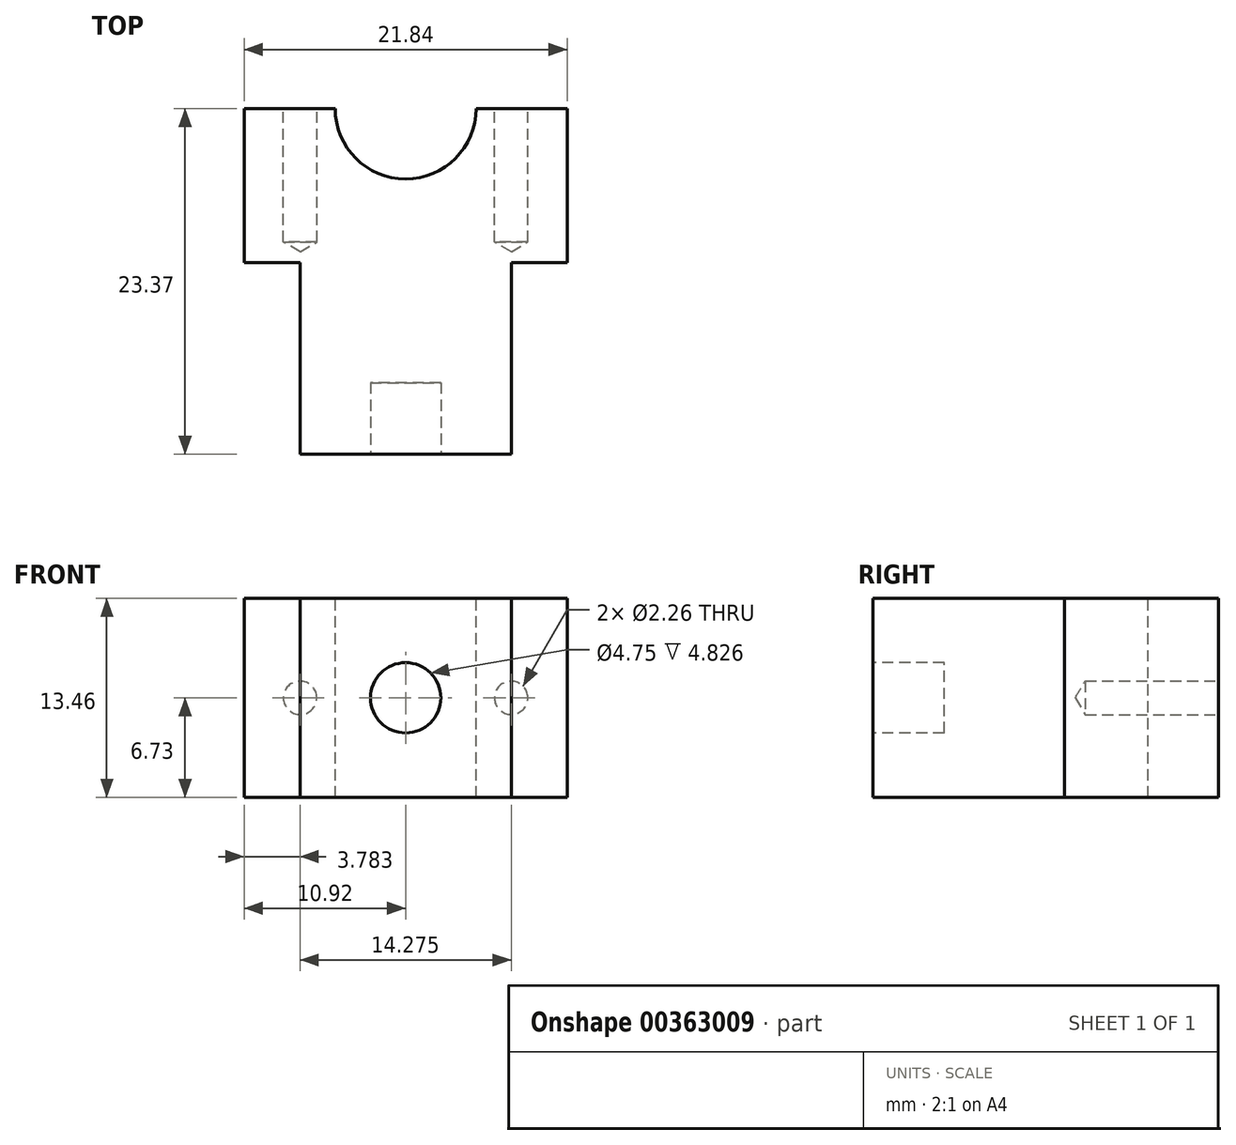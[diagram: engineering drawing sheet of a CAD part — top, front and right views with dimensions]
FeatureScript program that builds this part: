
annotation { "Feature Type Name" : "Feature", "Feature Type Description" : "" }
export const myFeature = defineFeature(function(context is Context, id is Id, definition is map)
    precondition{}
    {
        {
            var Q0;
            Q0=qCreatedBy(makeId("Front.planeOp"),FACE);
            var sketch = newSketch(context, id + "F0", { "sketchPlane" : qUnion([Q0])});
            skLineSegment(sketch, "E0.bottom", {"start": v(10.92, 6.73) * mm, "end": v(-10.92, 6.73) * mm});
            skLineSegment(sketch, "E0.top", {"start": v(10.92, -6.73) * mm, "end": v(-10.92, -6.73) * mm});
            skLineSegment(sketch, "E0.left", {"start": v(10.92, 6.73) * mm, "end": v(10.92, -6.73) * mm});
            skLineSegment(sketch, "E0.right", {"start": v(-10.92, 6.73) * mm, "end": v(-10.92, -6.73) * mm});
            skPoint(sketch, "E0.middle", {"position": v(0, 0) * mm});
            skSolve(sketch);
        }
        {
            var Q0;
            Q0=makeQuery(id+"F0.imprint","IMPRINT",FACE,{"disambiguationData":[TD([[makeQuery(id+"F0.imprint","IMPRINT",EDGE,{"derivedFrom":sQuery(id+"F0.wireOp",EDGE,"E0.bottom")}),1.0]])]});
            extrude(context, id + "F1", {"entities" : qUnion([Q0]), "depth" : 10.4 * mm});
        }
        {
            var Q0;
            Q0=makeQuery(id+"F1.opExtrude","CAP_FACE",FACE,{"disambiguationData":[OSD([sQuery(id+"F0.wireOp",EDGE,"E0.bottom"),sQuery(id+"F0.wireOp",EDGE,"E0.top"),sQuery(id+"F0.wireOp",EDGE,"E0.left"),sQuery(id+"F0.wireOp",EDGE,"E0.right")])],"isStart":false});
            var sketch = newSketch(context, id + "F2", { "sketchPlane" : qUnion([Q0])});
            skLineSegment(sketch, "E1.bottom", {"start": v(7.14, 6.73) * mm, "end": v(-7.14, 6.73) * mm});
            skLineSegment(sketch, "E1.top", {"start": v(7.14, -6.73) * mm, "end": v(-7.14, -6.73) * mm});
            skLineSegment(sketch, "E1.left", {"start": v(7.14, 6.73) * mm, "end": v(7.14, -6.73) * mm});
            skLineSegment(sketch, "E1.right", {"start": v(-7.14, 6.73) * mm, "end": v(-7.14, -6.73) * mm});
            skPoint(sketch, "E1.middle", {"position": v(0, 0) * mm});
            skSolve(sketch);
        }
        {
            var Q0;
            Q0=makeQuery(id+"F2.imprint","IMPRINT",FACE,{"disambiguationData":[TD([[makeQuery(id+"F2.imprint","IMPRINT",EDGE,{"derivedFrom":sQuery(id+"F2.wireOp",EDGE,"E1.bottom")}),1.0]])]});
            extrude(context, id + "F3", {"entities" : qUnion([Q0]), "operationType" : NewBodyOperationType.ADD, "depth" : 12.95 * mm});
        }
        {
            var Q0;
            Q0=makeQuery(id+"F3.opExtrude","CAP_FACE",FACE,{"disambiguationData":[OSD([sQuery(id+"F2.wireOp",EDGE,"E1.bottom"),sQuery(id+"F2.wireOp",EDGE,"E1.top"),sQuery(id+"F2.wireOp",EDGE,"E1.left"),sQuery(id+"F2.wireOp",EDGE,"E1.right")])],"isStart":false});
            var sketch = newSketch(context, id + "F4", { "sketchPlane" : qUnion([Q0])});
            skCircle(sketch, "E2", {"center": v(0, 0) * mm, "radius": 2.37 * mm});
            skSolve(sketch);
        }
        {
            var Q0;
            Q0=makeQuery(id+"F4.imprint","IMPRINT",FACE,{"disambiguationData":[TD([[makeQuery(id+"F4.imprint","IMPRINT",EDGE,{"derivedFrom":sQuery(id+"F4.wireOp",EDGE,"E2")}),1.0]])]});
            extrude(context, id + "F5", {"entities" : qUnion([Q0]), "operationType" : NewBodyOperationType.REMOVE, "oppositeDirection" : true, "depth" : 4.83 * mm});
        }
        {
            var Q0;
            Q0=makeQuery(id+"F1.opExtrude","CAP_FACE",FACE,{"disambiguationData":[OSD([sQuery(id+"F0.wireOp",EDGE,"E0.bottom"),sQuery(id+"F0.wireOp",EDGE,"E0.top"),sQuery(id+"F0.wireOp",EDGE,"E0.left"),sQuery(id+"F0.wireOp",EDGE,"E0.right")])],"isStart":true});
            var sketch = newSketch(context, id + "F6", { "sketchPlane" : qUnion([Q0])});
            skPoint(sketch, "E3", {"position": v(7.14, 0) * mm});
            skPoint(sketch, "E4", {"position": v(-7.14, 0) * mm});
            skSolve(sketch);
        }
        {
            var Q0;
            Q0=sQuery(id+"F6.wireOp",VERTEX,"E3");
            var Q1;
            Q1=sQuery(id+"F6.wireOp",VERTEX,"E4");
            var Q2;
            Q2=makeQuery(id+"F1.opExtrude","SWEPT_BODY",BODY,{"disambiguationData":[OSD([sQuery(id+"F0.wireOp",EDGE,"E0.bottom"),sQuery(id+"F0.wireOp",EDGE,"E0.top"),sQuery(id+"F0.wireOp",EDGE,"E0.left"),sQuery(id+"F0.wireOp",EDGE,"E0.right")])]});
            hole(context, id + "F7", {"style" : HoleStyle.SIMPLE, "endStyle" : HoleEndStyle.BLIND, "standardTappedOrClearance" : lookupTablePath({ "standard" : "ANSI", "engagement" : "75%", "pitch" : "40 tpi", "size" : "#4", "type" : "Tapped" }), "standardBlindInLast" : lookupTablePath({ "standard" : "ANSI", "engagement" : "75%", "pitch" : "40 tpi", "size" : "#4", "type" : "Tapped" }), "holeDiameter" : 2.26 * mm, "showTappedDepth" : true, "holeDepth" : 9.02 * mm, "tappedDepth" : 7.11 * mm, "tapClearance" : 3, "locations" : qUnion([Q0, Q1]), "scope" : qUnion([Q2]), "majorDiameter" : 2.84 * mm});
        }
        {
            var Q0;
            Q0=makeQuery(id+"F3.boolean.opBoolean","MERGE",FACE,{"derivedFrom":[makeQuery(id+"F1.opExtrude","SWEPT_FACE",FACE,{"disambiguationData":[OSD([sQuery(id+"F0.wireOp",EDGE,"E0.bottom")])]}),makeQuery(id+"F3.opExtrude","SWEPT_FACE",FACE,{"disambiguationData":[OSD([sQuery(id+"F2.wireOp",EDGE,"E1.bottom")])]})]});
            var sketch = newSketch(context, id + "F8", { "sketchPlane" : qUnion([Q0])});
            skCircle(sketch, "E5", {"center": v(0, 0) * mm, "radius": 4.76 * mm});
            skSolve(sketch);
        }
        {
            var Q0;
            {var subQ0=sQuery(id+"F8.wireOp",EDGE,"E5");var subQ1=makeQuery(id+"F1.opExtrude","CAP_EDGE",EDGE,{"disambiguationData":[OSD([sQuery(id+"F0.wireOp",EDGE,"E0.bottom")])],"isStart":true});var subQ2=makeQuery(id+"F8.imprint","INTERSECT",VERTEX,{"disambiguationData":[OD(0.0)],"derivedFrom":[subQ1,subQ0]});Q0=makeQuery(id+"F8.imprint","IMPRINT",FACE,{"disambiguationData":[TD([[makeQuery(id+"F8.imprint","IMPRINT",EDGE,{"disambiguationData":[TD([[subQ2,1.0]])],"derivedFrom":subQ0}),1.0]])]});}
            extrude(context, id + "F9", {"entities" : qUnion([Q0]), "operationType" : NewBodyOperationType.REMOVE, "endBound" : BoundingType.THROUGH_ALL, "oppositeDirection" : true, "depth" : 25.4 * mm});
        }
    });
